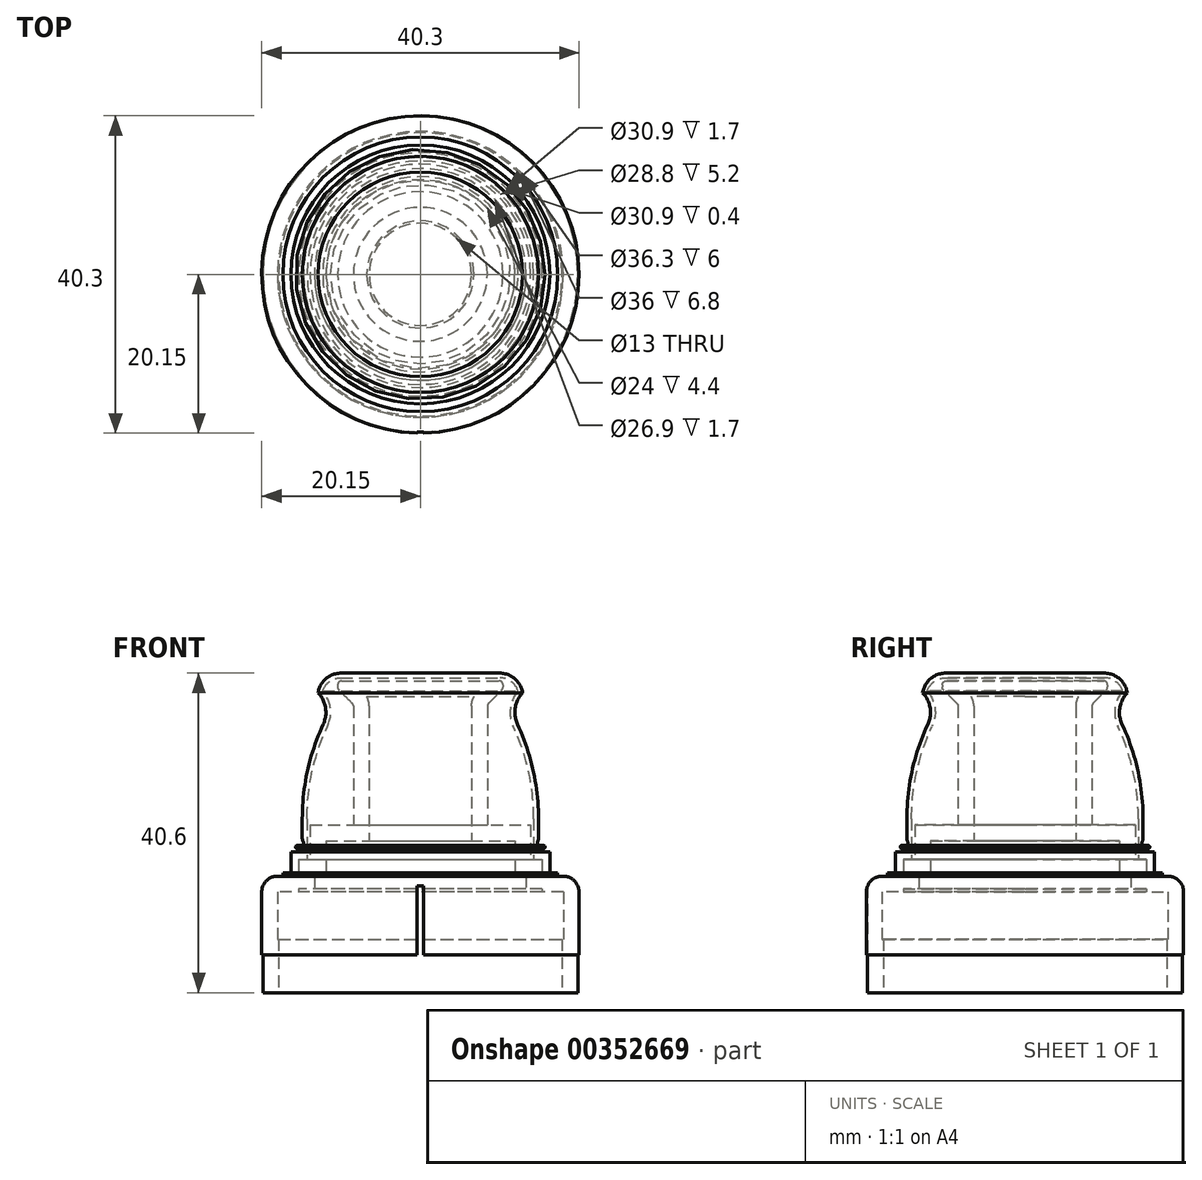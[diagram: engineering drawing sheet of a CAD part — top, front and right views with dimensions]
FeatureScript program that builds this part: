
annotation { "Feature Type Name" : "Feature", "Feature Type Description" : "" }
export const myFeature = defineFeature(function(context is Context, id is Id, definition is map)
    precondition{}
    {
        {
            var Q0;
            Q0=qCreatedBy(makeId("Front.planeOp"),FACE);
            var sketch = newSketch(context, id + "F0", { "sketchPlane" : qUnion([Q0])});
            skLineSegment(sketch, "E0", {"start": v(0, 0) * mm, "end": v(-20, 0) * mm});
            skLineSegment(sketch, "E1", {"start": v(-20, 0) * mm, "end": v(-20, 4.8) * mm});
            skLineSegment(sketch, "E2", {"start": v(-20, 4.8) * mm, "end": v(-20.15, 4.8) * mm});
            skLineSegment(sketch, "E3", {"start": v(-20.15, 4.8) * mm, "end": v(-20.15, 14.8) * mm});
            skLineSegment(sketch, "E4", {"start": v(-20.15, 14.8) * mm, "end": v(-17.45, 14.8) * mm});
            skLineSegment(sketch, "E5", {"start": v(-17.45, 14.8) * mm, "end": v(-17.45, 15.2) * mm});
            skLineSegment(sketch, "E6", {"start": v(-17.45, 15.2) * mm, "end": v(-16.45, 15.2) * mm});
            skLineSegment(sketch, "E7", {"start": v(-16.45, 15.2) * mm, "end": v(-16.45, 17.9) * mm});
            skLineSegment(sketch, "E8", {"start": v(-16.45, 17.9) * mm, "end": v(-15.05, 17.9) * mm});
            skLineSegment(sketch, "E9", {"start": v(-15.05, 17.9) * mm, "end": v(-15.05, 18.3) * mm});
            skLineSegment(sketch, "E10", {"start": v(-15.05, 18.3) * mm, "end": v(-15.85, 18.3) * mm});
            skLineSegment(sketch, "E11", {"start": v(-15.85, 18.3) * mm, "end": v(-15.85, 18.7) * mm});
            skLineSegment(sketch, "E12", {"start": v(-15.85, 18.7) * mm, "end": v(-14.85, 18.7) * mm});
            skLineSegment(sketch, "E13", {"start": v(-14.85, 18.7) * mm, "end": v(-14.85, 19.1) * mm});
            skLineSegment(sketch, "E14", {"start": v(-14.85, 19.1) * mm, "end": v(-15, 19.1) * mm});
            skLineSegment(sketch, "E15", {"start": v(-15, 19.1) * mm, "end": v(-15, 22.1) * mm});
            skLineSegment(sketch, "E16", {"start": v(0, 0) * mm, "end": v(0, 40.6) * mm});
            skLineSegment(sketch, "E17", {"start": v(0, 40.6) * mm, "end": v(-13, 40.6) * mm});
            skLineSegment(sketch, "E18", {"start": v(-13, 40.6) * mm, "end": v(-13, 38.1) * mm});
            skArc(sketch, "E19", {"start": v(-12.34, 34.1) * mm, "mid": v(-12.05, 36.2) * mm, "end": v(-13, 38.1) * mm});
            skArc(sketch, "E20", {"start": v(-12.34, 34.1) * mm, "mid": v(-14.33, 28.25) * mm, "end": v(-15, 22.1) * mm});
            skLineSegment(sketch, "E21", {"start": v(-16.45, 15.2) * mm, "end": v(0, 15.2) * mm});
            skLineSegment(sketch, "E22", {"start": v(0, 39.6) * mm, "end": v(-10, 39.6) * mm});
            skLineSegment(sketch, "E23", {"start": v(-10.5, 39.1) * mm, "end": v(-10.5, 38.8) * mm});
            skLineSegment(sketch, "E24", {"start": v(-10.5, 36.6) * mm, "end": v(-8.5, 36.6) * mm});
            skLineSegment(sketch, "E25", {"start": v(-8.5, 36.4) * mm, "end": v(-8.5, 21.3) * mm});
            skLineSegment(sketch, "E26", {"start": v(-8.5, 21.3) * mm, "end": v(-14, 21.3) * mm});
            skLineSegment(sketch, "E27", {"start": v(-14, 21.3) * mm, "end": v(-14, 16.9) * mm});
            skLineSegment(sketch, "E28", {"start": v(-14, 16.9) * mm, "end": v(-15.45, 16.9) * mm});
            skLineSegment(sketch, "E29", {"start": v(-15.45, 16.9) * mm, "end": v(-15.45, 15.2) * mm});
            skPoint(sketch, "E30.visualSharp", {"position": v(-10.5, 39.6) * mm});
            skArc(sketch, "E30.filletArc", {"start": v(-10, 39.6) * mm, "mid": v(-10.35, 39.45) * mm, "end": v(-10.5, 39.1) * mm});
            skLineSegment(sketch, "E31", {"start": v(-8.65, 36.75) * mm, "end": v(-10.35, 38.45) * mm});
            skPoint(sketch, "E32.newPointA", {"position": v(-10.5, 36.6) * mm});
            skPoint(sketch, "E32.newPointB", {"position": v(-10.5, 38.6) * mm});
            skArc(sketch, "E32.filletArc", {"start": v(-10.5, 38.8) * mm, "mid": v(-10.46, 38.62) * mm, "end": v(-10.35, 38.45) * mm});
            skPoint(sketch, "E33.visualSharp", {"position": v(-8.5, 36.6) * mm});
            skArc(sketch, "E33.filletArc", {"start": v(-8.5, 36.4) * mm, "mid": v(-8.54, 36.58) * mm, "end": v(-8.65, 36.75) * mm});
            skLineSegment(sketch, "E34.0", {"start": v(0, 40) * mm, "end": v(-12.4, 40) * mm});
            skLineSegment(sketch, "E34.1", {"start": v(-14.4, 16.9) * mm, "end": v(-14.4, 22.1) * mm});
            skArc(sketch, "E34.2", {"start": v(-11.8, 33.85) * mm, "mid": v(-13.74, 28.12) * mm, "end": v(-14.4, 22.1) * mm});
            skArc(sketch, "E34.3", {"start": v(-11.8, 33.85) * mm, "mid": v(-11.44, 36.18) * mm, "end": v(-12.4, 38.33) * mm});
            skLineSegment(sketch, "E34.4", {"start": v(-12.4, 40) * mm, "end": v(-12.4, 38.33) * mm});
            skSolve(sketch);
        }
        {
            var Q0;
            {var subQ5=sQuery(id+"F0.wireOp",EDGE,"E0");Q0=makeQuery(id+"F0.imprint","IMPRINT",FACE,{"disambiguationData":[TD([[makeQuery(id+"F0.imprint","IMPRINT",EDGE,{"derivedFrom":subQ5}),-1.0]])]});}
            var Q1;
            {var subQ5=sQuery(id+"F0.wireOp",EDGE,"E22");Q1=makeQuery(id+"F0.imprint","IMPRINT",FACE,{"disambiguationData":[TD([[makeQuery(id+"F0.imprint","IMPRINT",EDGE,{"derivedFrom":subQ5}),1.0]])]});}
            var Q2;
            Q2=sQuery(id+"F0.wireOp",EDGE,"E16");
            revolve(context, id + "F1", {"entities" : qUnion([Q0, Q1]), "axis" : qUnion([Q2]), "revolveType" : RevolveType.FULL});
        }
        {
            var Q0;
            {var subQ3=sQuery(id+"F0.wireOp",EDGE,"E7");Q0=makeQuery(id+"F0.imprint","IMPRINT",FACE,{"disambiguationData":[TD([[makeQuery(id+"F0.imprint","IMPRINT",EDGE,{"derivedFrom":subQ3}),-1.0]])]});}
            var Q1;
            Q1=sQuery(id+"F0.wireOp",EDGE,"E16");
            revolve(context, id + "F2", {"entities" : qUnion([Q0]), "axis" : qUnion([Q1]), "revolveType" : RevolveType.FULL});
        }
        {
            var Q0;
            Q0=makeQuery(id+"F2.opRevolve","SWEPT_EDGE",EDGE,{"disambiguationData":[OSD([sQuery(id+"F0.wireOp",EDGE,"E34.0"),sQuery(id+"F0.wireOp",EDGE,"E34.4")])]});
            fillet(context, id + "F3", {"entities" : qUnion([Q0]), "radius" : 2.4 * mm, "tangentPropagation" : true, "allowEdgeOverflow" : false});
        }
        {
            var Q0;
            Q0=makeQuery(id+"F2.opRevolve","SWEPT_EDGE",EDGE,{"disambiguationData":[OSD([sQuery(id+"F0.wireOp",EDGE,"E17"),sQuery(id+"F0.wireOp",EDGE,"E18")])]});
            fillet(context, id + "F4", {"entities" : qUnion([Q0]), "radius" : 3 * mm, "tangentPropagation" : true, "allowEdgeOverflow" : false});
        }
        {
            var Q0;
            Q0=makeQuery(id+"F2.opRevolve","SWEPT_EDGE",EDGE,{"disambiguationData":[OSD([sQuery(id+"F0.wireOp",EDGE,"E14"),sQuery(id+"F0.wireOp",EDGE,"E15")])]});
            fillet(context, id + "F5", {"entities" : qUnion([Q0]), "radius" : 1 * mm, "tangentPropagation" : true, "allowEdgeOverflow" : false});
        }
        {
            var Q0;
            Q0=makeQuery(id+"F5.opFillet","BLEND_EDGE",EDGE,{"blendedFrom":[makeQuery(id+"F2.opRevolve","SWEPT_EDGE",EDGE,{"disambiguationData":[OSD([sQuery(id+"F0.wireOp",EDGE,"E14"),sQuery(id+"F0.wireOp",EDGE,"E15")])]}),makeQuery(id+"F2.opRevolve","SWEPT_FACE",FACE,{"disambiguationData":[OSD([sQuery(id+"F0.wireOp",EDGE,"E13")])]})],"blendedInto":[makeQuery(id+"F2.opRevolve","SWEPT_FACE",FACE,{"disambiguationData":[OSD([sQuery(id+"F0.wireOp",EDGE,"E13")])]})]});
            var Q1;
            Q1=makeQuery(id+"F2.opRevolve","SWEPT_EDGE",EDGE,{"disambiguationData":[OSD([sQuery(id+"F0.wireOp",EDGE,"E12"),sQuery(id+"F0.wireOp",EDGE,"E13")])]});
            fillet(context, id + "F6", {"entities" : qUnion([Q0, Q1]), "radius" : .28 * mm, "tangentPropagation" : true, "allowEdgeOverflow" : false});
        }
        {
            var Q0;
            Q0=makeQuery(id+"F2.opRevolve","SWEPT_EDGE",EDGE,{"disambiguationData":[OSD([sQuery(id+"F0.wireOp",EDGE,"E11"),sQuery(id+"F0.wireOp",EDGE,"E12")])]});
            var Q1;
            Q1=makeQuery(id+"F2.opRevolve","SWEPT_EDGE",EDGE,{"disambiguationData":[OSD([sQuery(id+"F0.wireOp",EDGE,"E10"),sQuery(id+"F0.wireOp",EDGE,"E11")])]});
            var Q2;
            Q2=makeQuery(id+"F2.opRevolve","SWEPT_EDGE",EDGE,{"disambiguationData":[OSD([sQuery(id+"F0.wireOp",EDGE,"E9"),sQuery(id+"F0.wireOp",EDGE,"E10")])]});
            var Q3;
            Q3=makeQuery(id+"F2.opRevolve","SWEPT_EDGE",EDGE,{"disambiguationData":[OSD([sQuery(id+"F0.wireOp",EDGE,"E8"),sQuery(id+"F0.wireOp",EDGE,"E9")])]});
            fillet(context, id + "F7", {"entities" : qUnion([Q0, Q1, Q2, Q3]), "radius" : .2 * mm, "tangentPropagation" : true, "allowEdgeOverflow" : false});
        }
        {
            var Q0;
            Q0=makeQuery(id+"F1.opRevolve","SWEPT_EDGE",EDGE,{"disambiguationData":[OSD([sQuery(id+"F0.wireOp",EDGE,"E3"),sQuery(id+"F0.wireOp",EDGE,"E4")])]});
            fillet(context, id + "F8", {"entities" : qUnion([Q0]), "radius" : 2 * mm, "tangentPropagation" : true, "allowEdgeOverflow" : false});
        }
        {
            var Q0;
            Q0=makeQuery(id+"F1.opRevolve","SWEPT_FACE",FACE,{"disambiguationData":[OSD([sQuery(id+"F0.wireOp",EDGE,"E0")])]});
            shell(context, id + "F9", {"entities" : qUnion([Q0]), "thickness" : 2 * mm});
        }
        {
            var Q0;
            Q0=qCreatedBy(makeId("Top.planeOp"),FACE);
            var sketch = newSketch(context, id + "F10", { "sketchPlane" : qUnion([Q0])});
            skLineSegment(sketch, "E35.bottom", {"start": v(-0.4, -21) * mm, "end": v(0.4, -21) * mm});
            skLineSegment(sketch, "E35.left", {"start": v(-0.4, -21) * mm, "end": v(-0.4, -20) * mm});
            skLineSegment(sketch, "E35.right", {"start": v(0.4, -21) * mm, "end": v(0.4, -20) * mm});
            skLineSegment(sketch, "E36", {"start": v(0, 0) * mm, "end": v(0, -20) * mm, "construction": true});
            skArc(sketch, "E37", {"start": v(-0.4, -20) * mm, "mid": v(0, -20) * mm, "end": v(0.4, -20) * mm});
            skLineSegment(sketch, "E38", {"start": v(-0.4, -20) * mm, "end": v(-0.4, -20) * mm});
            skLineSegment(sketch, "E39", {"start": v(0.4, -20) * mm, "end": v(0.4, -20) * mm});
            skPoint(sketch, "E40", {"position": v(0, -21) * mm});
            skSolve(sketch);
        }
        {
            var Q0;
            Q0=makeQuery(id+"F10.imprint","IMPRINT",FACE,{"disambiguationData":[TD([[makeQuery(id+"F10.imprint","IMPRINT",EDGE,{"derivedFrom":sQuery(id+"F10.wireOp",EDGE,"E35.bottom")}),1.0]])]});
            extrude(context, id + "F11", {"entities" : qUnion([Q0]), "operationType" : NewBodyOperationType.REMOVE, "endBound" : BoundingType.THROUGH_ALL, "depth" : 25 * mm});
        }
    });
